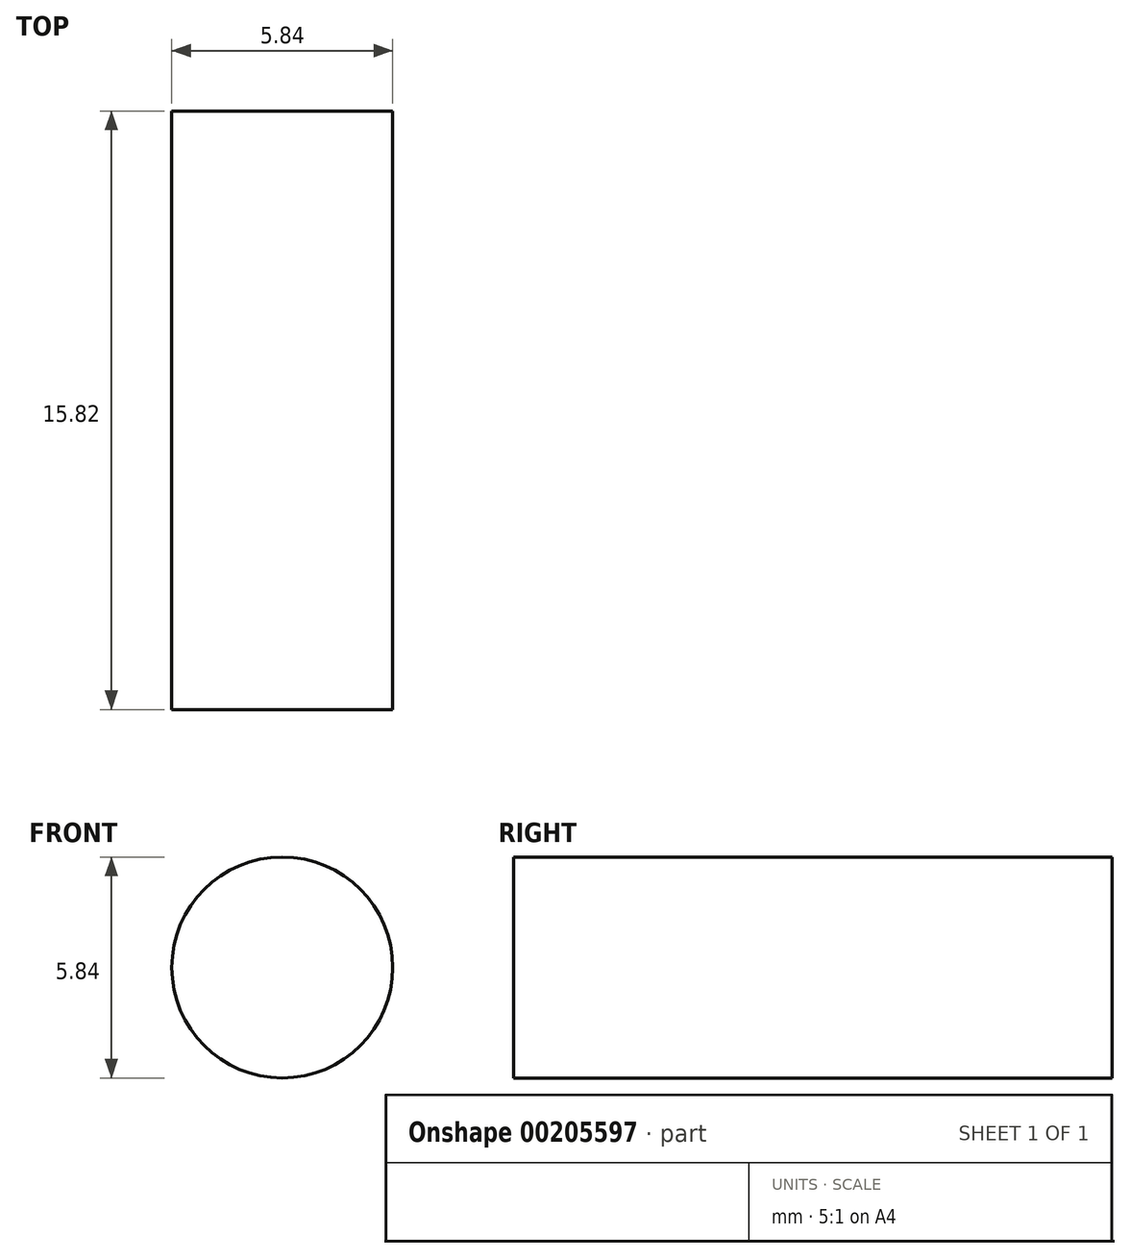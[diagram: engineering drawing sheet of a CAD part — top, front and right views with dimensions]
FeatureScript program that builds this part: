
annotation { "Feature Type Name" : "Feature", "Feature Type Description" : "" }
export const myFeature = defineFeature(function(context is Context, id is Id, definition is map)
    precondition{}
    {
        {
            var Q0;
            Q0=qCreatedBy(makeId("Front.planeOp"),FACE);
            var sketch = newSketch(context, id + "F0", { "sketchPlane" : qUnion([Q0])});
            skCircle(sketch, "E0", {"center": v(0, 0) * mm, "radius": 2.92 * mm});
            skSolve(sketch);
        }
        {
            var Q0;
            Q0=qSketchRegion(id+"F0",true);
            extrude(context, id + "F1", {"entities" : qUnion([Q0]), "depth" : 15.82 * mm});
        }
    });
